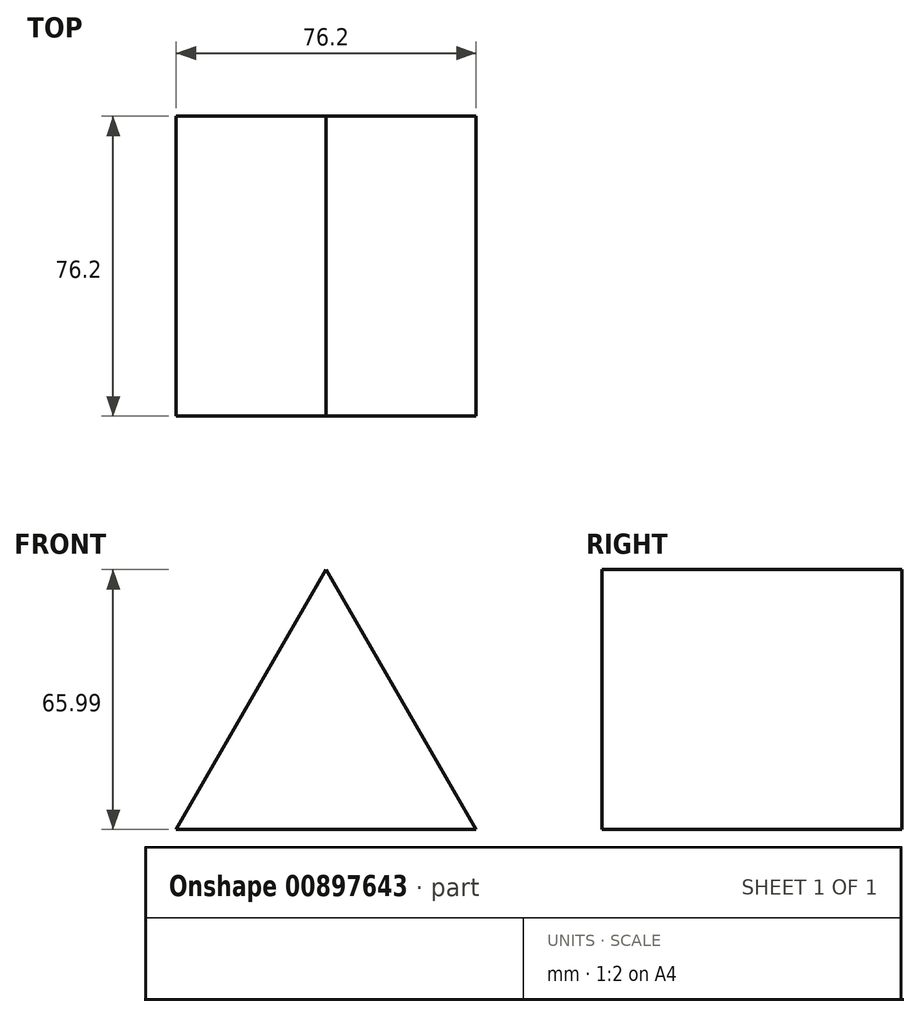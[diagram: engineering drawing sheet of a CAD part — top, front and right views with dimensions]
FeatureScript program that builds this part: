
annotation { "Feature Type Name" : "Feature", "Feature Type Description" : "" }
export const myFeature = defineFeature(function(context is Context, id is Id, definition is map)
    precondition{}
    {
        {
            var Q0;
            Q0=qCreatedBy(makeId("Front.planeOp"),FACE);
            var sketch = newSketch(context, id + "F0", { "sketchPlane" : qUnion([Q0])});
            skLineSegment(sketch, "E0", {"start": v(0, 47.83) * mm, "end": v(-38.1, -18.16) * mm});
            skLineSegment(sketch, "E1", {"start": v(-38.1, -18.16) * mm, "end": v(38.1, -18.16) * mm});
            skLineSegment(sketch, "E2", {"start": v(38.1, -18.16) * mm, "end": v(0, 47.83) * mm});
            skSolve(sketch);
        }
        {
            var Q0;
            Q0 = qSketchRegion(id + "F0", true);
            extrude(context, id + "F1", {"entities" : qUnion([Q0]), "depth" : 76.2 * mm, "offsetDistance" : 25.4 * mm});
        }
    });
